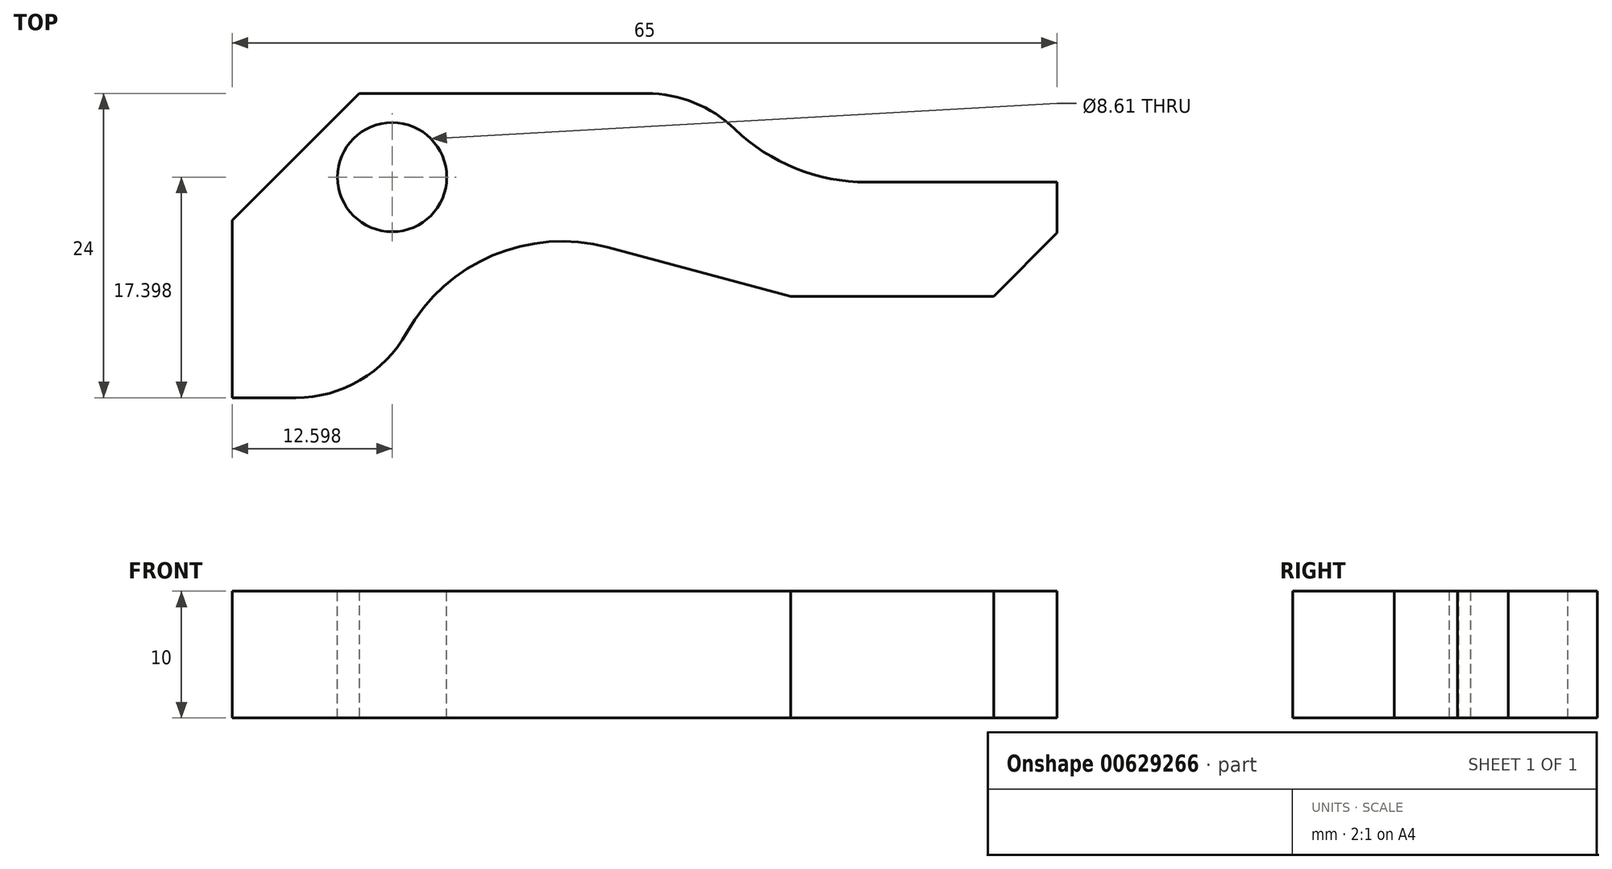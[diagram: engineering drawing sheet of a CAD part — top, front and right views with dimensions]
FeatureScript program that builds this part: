
annotation { "Feature Type Name" : "Feature", "Feature Type Description" : "" }
export const myFeature = defineFeature(function(context is Context, id is Id, definition is map)
    precondition{}
    {
        {
            var Q0;
            Q0=qCreatedBy(makeId("Top.planeOp"),FACE);
            var sketch = newSketch(context, id + "F0", { "sketchPlane" : qUnion([Q0])});
            skLineSegment(sketch, "E0", {"start": v(-29.6, -11.86) * mm, "end": v(-29.6, 2.14) * mm});
            skLineSegment(sketch, "E1", {"start": v(-29.6, 2.14) * mm, "end": v(-19.6, 12.14) * mm});
            skLineSegment(sketch, "E2", {"start": v(-19.6, 12.14) * mm, "end": v(3.05, 12.14) * mm});
            skArc(sketch, "E3", {"start": v(3.05, 12.14) * mm, "mid": v(6.8, 11.41) * mm, "end": v(10, 9.34) * mm});
            skArc(sketch, "E4", {"start": v(10, 9.34) * mm, "mid": v(14.79, 6.23) * mm, "end": v(20.4, 5.14) * mm});
            skLineSegment(sketch, "E5", {"start": v(20.4, 5.14) * mm, "end": v(35.4, 5.14) * mm});
            skLineSegment(sketch, "E6", {"start": v(35.4, 5.14) * mm, "end": v(35.4, 1.14) * mm});
            skLineSegment(sketch, "E7", {"start": v(35.4, 1.14) * mm, "end": v(30.4, -3.86) * mm});
            skLineSegment(sketch, "E8", {"start": v(30.4, -3.86) * mm, "end": v(14.4, -3.86) * mm});
            skLineSegment(sketch, "E9", {"start": v(14.4, -3.86) * mm, "end": v(0, 0) * mm});
            skArc(sketch, "E10", {"start": v(0, 0) * mm, "mid": v(-9.08, -0.63) * mm, "end": v(-15.86, -6.72) * mm});
            skArc(sketch, "E11", {"start": v(-15.86, -6.72) * mm, "mid": v(-19.53, -10.48) * mm, "end": v(-24.6, -11.86) * mm});
            skLineSegment(sketch, "E12", {"start": v(-24.6, -11.86) * mm, "end": v(-29.6, -11.86) * mm});
            skSolve(sketch);
        }
        {
            var Q0;
            Q0 = qSketchRegion(id + "F0", true);
            extrude(context, id + "F1", {"entities" : qUnion([Q0]), "depth" : 10 * mm, "offsetDistance" : 25 * mm});
        }
        {
            var Q0;
            Q0=makeQuery(id+"F1.opExtrude","CAP_FACE",FACE,{"disambiguationData":[OSD([sQuery(id+"F0.wireOp",EDGE,"E0"),sQuery(id+"F0.wireOp",EDGE,"E1"),sQuery(id+"F0.wireOp",EDGE,"E2"),sQuery(id+"F0.wireOp",EDGE,"E3"),sQuery(id+"F0.wireOp",EDGE,"E4"),sQuery(id+"F0.wireOp",EDGE,"E5"),sQuery(id+"F0.wireOp",EDGE,"E6"),sQuery(id+"F0.wireOp",EDGE,"E7"),sQuery(id+"F0.wireOp",EDGE,"E8"),sQuery(id+"F0.wireOp",EDGE,"E9"),sQuery(id+"F0.wireOp",EDGE,"E10"),sQuery(id+"F0.wireOp",EDGE,"E11"),sQuery(id+"F0.wireOp",EDGE,"E12")])],"isStart":false});
            var sketch = newSketch(context, id + "F2", { "sketchPlane" : qUnion([Q0])});
            skCircle(sketch, "E13", {"center": v(-17, 5.54) * mm, "radius": 4.3 * mm});
            skSolve(sketch);
        }
        {
            var Q0;
            Q0 = qSketchRegion(id + "F2", true);
            extrude(context, id + "F3", {"entities" : qUnion([Q0]), "operationType" : NewBodyOperationType.REMOVE, "oppositeDirection" : true, "depth" : 25 * mm, "offsetDistance" : 25 * mm});
        }
    });
